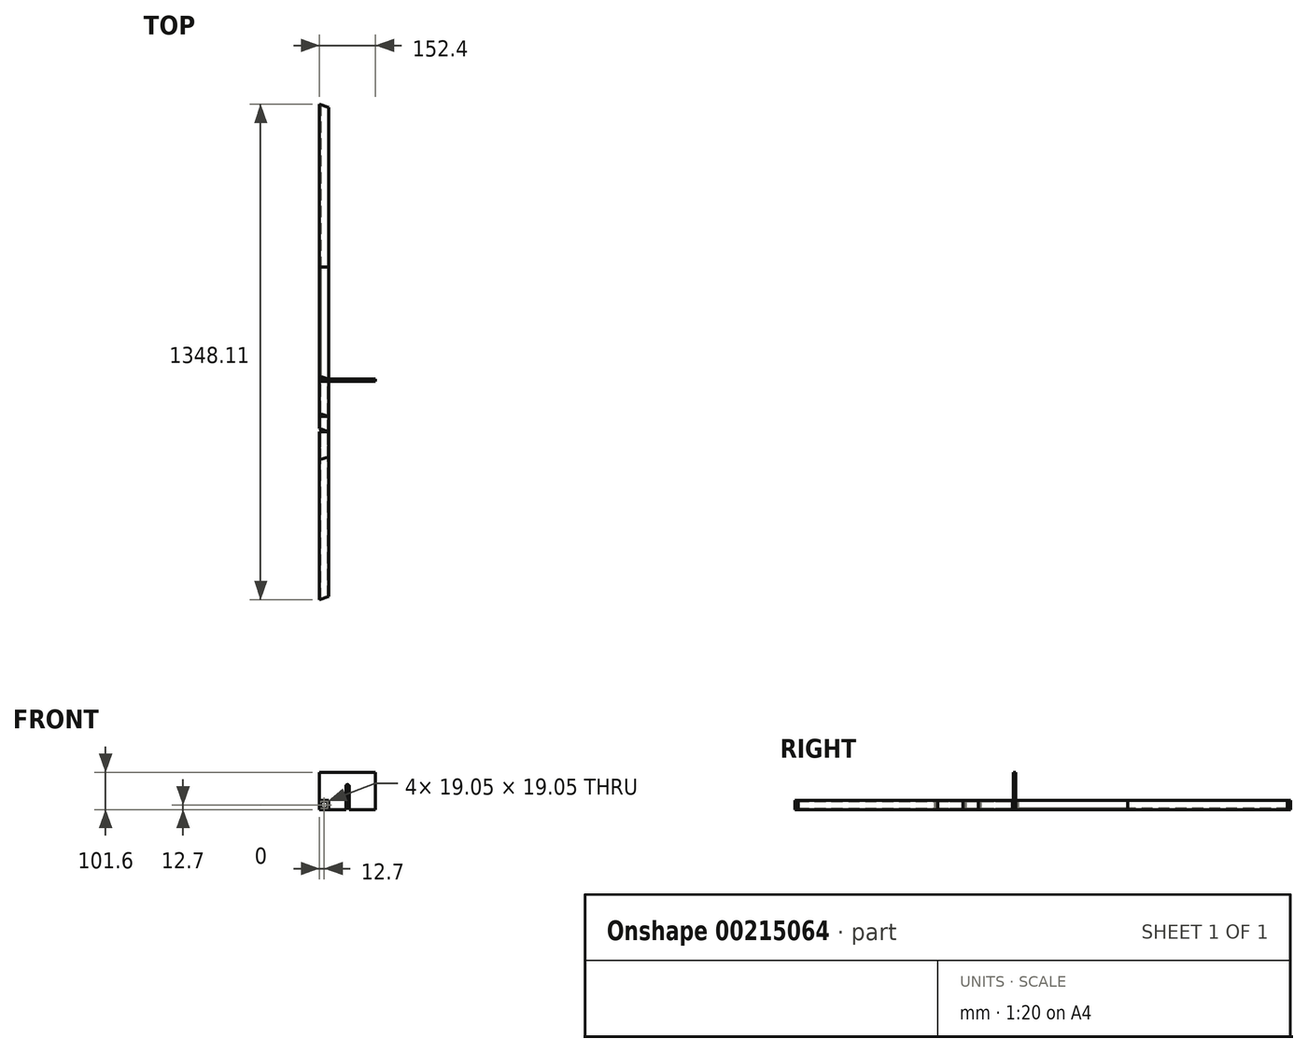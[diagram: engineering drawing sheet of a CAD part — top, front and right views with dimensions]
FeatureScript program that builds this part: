
annotation { "Feature Type Name" : "Feature", "Feature Type Description" : "" }
export const myFeature = defineFeature(function(context is Context, id is Id, definition is map)
    precondition{}
    {
        {
            var Q0;
            Q0=qCreatedBy(makeId("Front.planeOp"),FACE);
            var sketch = newSketch(context, id + "F0", { "sketchPlane" : qUnion([Q0])});
            skLineSegment(sketch, "E0.bottom", {"start": v(0, 0) * mm, "end": v(25.4, 0) * mm});
            skLineSegment(sketch, "E0.top", {"start": v(0, 25.4) * mm, "end": v(25.4, 25.4) * mm});
            skLineSegment(sketch, "E0.left", {"start": v(0, 0) * mm, "end": v(0, 25.4) * mm});
            skLineSegment(sketch, "E0.right", {"start": v(25.4, 0) * mm, "end": v(25.4, 25.4) * mm});
            skLineSegment(sketch, "E1.bottom", {"start": v(3.18, 3.18) * mm, "end": v(22.23, 3.18) * mm});
            skLineSegment(sketch, "E1.top", {"start": v(3.17, 22.23) * mm, "end": v(22.22, 22.23) * mm});
            skLineSegment(sketch, "E1.left", {"start": v(3.17, 3.18) * mm, "end": v(3.17, 22.23) * mm});
            skLineSegment(sketch, "E1.right", {"start": v(22.23, 3.18) * mm, "end": v(22.22, 22.23) * mm});
            skSolve(sketch);
        }
        {
            var Q0;
            Q0 = qSketchRegion(id + "F0", true);
            extrude(context, id + "F1", {"entities" : qUnion([Q0]), "oppositeDirection" : true, "depth" : 748.03 * mm, "offsetDistance" : 25.4 * mm});
        }
        {
            var Q0;
            Q0=makeQuery(id+"F1.opExtrude","SWEPT_FACE",FACE,{"disambiguationData":[OSD([sQuery(id+"F0.wireOp",EDGE,"E0.top")])]});
            var sketch = newSketch(context, id + "F2", { "sketchPlane" : qUnion([Q0])});
            skLineSegment(sketch, "E2", {"start": v(0, 0) * mm, "end": v(25.4, 0) * mm});
            skLineSegment(sketch, "E3", {"start": v(25.4, 0) * mm, "end": v(0, 8.25) * mm});
            skLineSegment(sketch, "E4", {"start": v(0, 8.25) * mm, "end": v(0, 0) * mm});
            skLineSegment(sketch, "E5", {"start": v(25.4, 748.03) * mm, "end": v(0, 748.03) * mm});
            skLineSegment(sketch, "E6", {"start": v(0, 748.03) * mm, "end": v(25.4, 739.78) * mm});
            skLineSegment(sketch, "E7", {"start": v(25.4, 739.78) * mm, "end": v(25.4, 748.03) * mm});
            skSolve(sketch);
        }
        {
            var Q0;
            Q0 = qSketchRegion(id + "F2", true);
            var Q1;
            Q1=makeQuery(id+"F1.opExtrude","SWEPT_FACE",FACE,{"disambiguationData":[OSD([sQuery(id+"F0.wireOp",EDGE,"E0.bottom")])]});
            extrude(context, id + "F3", {"entities" : qUnion([Q0]), "operationType" : NewBodyOperationType.REMOVE, "endBound" : BoundingType.UP_TO_SURFACE, "oppositeDirection" : true, "depth" : 25.4 * mm, "endBoundEntityFace" : qUnion([Q1]), "offsetDistance" : 25.4 * mm});
        }
        {
            var Q0;
            Q0=qCreatedBy(makeId("Front.planeOp"),FACE);
            var sketch = newSketch(context, id + "F4", { "sketchPlane" : qUnion([Q0])});
            skLineSegment(sketch, "E8.bottom", {"start": v(0, 0) * mm, "end": v(25.4, 0) * mm});
            skLineSegment(sketch, "E8.top", {"start": v(0, 25.4) * mm, "end": v(25.4, 25.4) * mm});
            skLineSegment(sketch, "E8.left", {"start": v(0, 0) * mm, "end": v(0, 25.4) * mm});
            skLineSegment(sketch, "E8.right", {"start": v(25.4, 0) * mm, "end": v(25.4, 25.4) * mm});
            skLineSegment(sketch, "E9.bottom", {"start": v(3.18, 3.18) * mm, "end": v(22.23, 3.18) * mm});
            skLineSegment(sketch, "E9.top", {"start": v(3.17, 22.22) * mm, "end": v(22.22, 22.22) * mm});
            skLineSegment(sketch, "E9.left", {"start": v(3.17, 3.18) * mm, "end": v(3.17, 22.22) * mm});
            skLineSegment(sketch, "E9.right", {"start": v(22.23, 3.18) * mm, "end": v(22.22, 22.22) * mm});
            skSolve(sketch);
        }
        {
            var Q0;
            Q0 = qSketchRegion(id + "F4", true);
            extrude(context, id + "F5", {"entities" : qUnion([Q0]), "depth" : 219.71 * mm, "offsetDistance" : 25.4 * mm});
        }
        {
            var Q0;
            Q0=makeQuery(id+"F5.opExtrude","SWEPT_FACE",FACE,{"disambiguationData":[OSD([sQuery(id+"F4.wireOp",EDGE,"E8.top")])]});
            var sketch = newSketch(context, id + "F6", { "sketchPlane" : qUnion([Q0])});
            skLineSegment(sketch, "E10", {"start": v(0, -219.71) * mm, "end": v(25.4, -219.71) * mm});
            skLineSegment(sketch, "E11", {"start": v(25.4, -219.71) * mm, "end": v(25.4, -211.46) * mm});
            skLineSegment(sketch, "E12", {"start": v(25.4, -211.46) * mm, "end": v(0, -219.71) * mm});
            skLineSegment(sketch, "E13", {"start": v(25.4, 0) * mm, "end": v(25.4, -8.25) * mm});
            skLineSegment(sketch, "E14", {"start": v(25.4, -8.25) * mm, "end": v(0, 0) * mm});
            skLineSegment(sketch, "E15", {"start": v(0, 0) * mm, "end": v(25.4, 0) * mm});
            skSolve(sketch);
        }
        {
            var Q0;
            Q0 = qSketchRegion(id + "F6", true);
            var Q1;
            Q1=makeQuery(id+"F5.opExtrude","SWEPT_FACE",FACE,{"disambiguationData":[OSD([sQuery(id+"F4.wireOp",EDGE,"E8.bottom")])]});
            extrude(context, id + "F7", {"entities" : qUnion([Q0]), "operationType" : NewBodyOperationType.REMOVE, "endBound" : BoundingType.UP_TO_SURFACE, "oppositeDirection" : true, "depth" : 25.4 * mm, "endBoundEntityFace" : qUnion([Q1]), "offsetDistance" : 25.4 * mm});
        }
        {
            var Q0;
            Q0=qCreatedBy(makeId("Front.planeOp"),FACE);
            var sketch = newSketch(context, id + "F8", { "sketchPlane" : qUnion([Q0])});
            skLineSegment(sketch, "E16.bottom", {"start": v(0, 0) * mm, "end": v(25.4, 0) * mm});
            skLineSegment(sketch, "E16.top", {"start": v(0, 25.4) * mm, "end": v(25.4, 25.4) * mm});
            skLineSegment(sketch, "E16.left", {"start": v(0, 0) * mm, "end": v(0, 25.4) * mm});
            skLineSegment(sketch, "E16.right", {"start": v(25.4, 0) * mm, "end": v(25.4, 25.4) * mm});
            skLineSegment(sketch, "E17.bottom", {"start": v(3.17, 3.18) * mm, "end": v(22.22, 3.18) * mm});
            skLineSegment(sketch, "E17.top", {"start": v(3.17, 22.22) * mm, "end": v(22.22, 22.22) * mm});
            skLineSegment(sketch, "E17.left", {"start": v(3.17, 3.18) * mm, "end": v(3.17, 22.22) * mm});
            skLineSegment(sketch, "E17.right", {"start": v(22.22, 3.18) * mm, "end": v(22.22, 22.22) * mm});
            skSolve(sketch);
        }
        {
            var Q0;
            Q0 = qSketchRegion(id + "F8", true);
            extrude(context, id + "F9", {"entities" : qUnion([Q0]), "oppositeDirection" : true, "depth" : 304.8 * mm, "offsetDistance" : 25.4 * mm});
        }
        {
            var Q0;
            Q0=qCreatedBy(makeId("Front.planeOp"),FACE);
            var sketch = newSketch(context, id + "F10", { "sketchPlane" : qUnion([Q0])});
            skLineSegment(sketch, "E18.bottom", {"start": v(0, 0) * mm, "end": v(25.4, 0) * mm});
            skLineSegment(sketch, "E18.top", {"start": v(0, 25.4) * mm, "end": v(25.4, 25.4) * mm});
            skLineSegment(sketch, "E18.left", {"start": v(0, 0) * mm, "end": v(0, 25.4) * mm});
            skLineSegment(sketch, "E18.right", {"start": v(25.4, 0) * mm, "end": v(25.4, 25.4) * mm});
            skLineSegment(sketch, "E19.bottom", {"start": v(3.17, 22.22) * mm, "end": v(22.22, 22.22) * mm});
            skLineSegment(sketch, "E19.top", {"start": v(3.17, 3.18) * mm, "end": v(22.22, 3.18) * mm});
            skLineSegment(sketch, "E19.left", {"start": v(3.17, 22.22) * mm, "end": v(3.17, 3.18) * mm});
            skLineSegment(sketch, "E19.right", {"start": v(22.22, 22.22) * mm, "end": v(22.23, 3.18) * mm});
            skSolve(sketch);
        }
        {
            var Q0;
            Q0 = qSketchRegion(id + "F10", true);
            extrude(context, id + "F11", {"entities" : qUnion([Q0]), "depth" : 600.07 * mm, "offsetDistance" : 25.4 * mm});
        }
        {
            var Q0;
            Q0=makeQuery(id+"F11.opExtrude","SWEPT_FACE",FACE,{"disambiguationData":[OSD([sQuery(id+"F10.wireOp",EDGE,"E18.top")])]});
            var sketch = newSketch(context, id + "F12", { "sketchPlane" : qUnion([Q0])});
            skLineSegment(sketch, "E20", {"start": v(0, 0) * mm, "end": v(25.4, -8.25) * mm});
            skLineSegment(sketch, "E21", {"start": v(25.4, -8.25) * mm, "end": v(25.4, 0) * mm});
            skLineSegment(sketch, "E22", {"start": v(25.4, 0) * mm, "end": v(0, 0) * mm});
            skLineSegment(sketch, "E23", {"start": v(0, -600.08) * mm, "end": v(25.4, -591.82) * mm});
            skLineSegment(sketch, "E24", {"start": v(25.4, -591.82) * mm, "end": v(25.4, -600.08) * mm});
            skLineSegment(sketch, "E25", {"start": v(25.4, -600.08) * mm, "end": v(0, -600.08) * mm});
            skSolve(sketch);
        }
        {
            var Q0;
            Q0 = qSketchRegion(id + "F12", true);
            var Q1;
            Q1=makeQuery(id+"F11.opExtrude","SWEPT_FACE",FACE,{"disambiguationData":[OSD([sQuery(id+"F10.wireOp",EDGE,"E18.bottom")])]});
            extrude(context, id + "F13", {"entities" : qUnion([Q0]), "operationType" : NewBodyOperationType.REMOVE, "endBound" : BoundingType.UP_TO_SURFACE, "oppositeDirection" : true, "depth" : 25.4 * mm, "endBoundEntityFace" : qUnion([Q1]), "offsetDistance" : 25.4 * mm});
        }
        {
            var Q0;
            Q0=qCreatedBy(makeId("Front.planeOp"),FACE);
            var sketch = newSketch(context, id + "F14", { "sketchPlane" : qUnion([Q0])});
            skLineSegment(sketch, "E26.bottom", {"start": v(0, 0) * mm, "end": v(25.4, 0) * mm});
            skLineSegment(sketch, "E26.top", {"start": v(0, 25.4) * mm, "end": v(25.4, 25.4) * mm});
            skLineSegment(sketch, "E26.left", {"start": v(0, 0) * mm, "end": v(0, 25.4) * mm});
            skLineSegment(sketch, "E26.right", {"start": v(25.4, 0) * mm, "end": v(25.4, 25.4) * mm});
            skLineSegment(sketch, "E27.bottom", {"start": v(3.18, 3.17) * mm, "end": v(22.22, 3.17) * mm});
            skLineSegment(sketch, "E27.top", {"start": v(3.17, 22.22) * mm, "end": v(22.22, 22.22) * mm});
            skLineSegment(sketch, "E27.left", {"start": v(3.18, 3.18) * mm, "end": v(3.17, 22.22) * mm});
            skLineSegment(sketch, "E27.right", {"start": v(22.22, 3.18) * mm, "end": v(22.22, 22.22) * mm});
            skSolve(sketch);
        }
        {
            var Q0;
            Q0 = qSketchRegion(id + "F14", true);
            extrude(context, id + "F15", {"entities" : qUnion([Q0]), "depth" : 101.58 * mm, "offsetDistance" : 25.4 * mm});
        }
        {
            var Q0;
            Q0=makeQuery(id+"F15.opExtrude","SWEPT_FACE",FACE,{"disambiguationData":[OSD([sQuery(id+"F14.wireOp",EDGE,"E26.top")])]});
            var sketch = newSketch(context, id + "F16", { "sketchPlane" : qUnion([Q0])});
            skLineSegment(sketch, "E28", {"start": v(25.4, -101.58) * mm, "end": v(0, -101.58) * mm});
            skLineSegment(sketch, "E29", {"start": v(0, -101.58) * mm, "end": v(0, -93.33) * mm});
            skLineSegment(sketch, "E30", {"start": v(0, -93.33) * mm, "end": v(25.4, -101.58) * mm});
            skSolve(sketch);
        }
        {
            var Q0;
            Q0 = qSketchRegion(id + "F16", true);
            extrude(context, id + "F17", {"entities" : qUnion([Q0]), "operationType" : NewBodyOperationType.REMOVE, "endBound" : BoundingType.THROUGH_ALL, "oppositeDirection" : true, "depth" : 25.4 * mm, "offsetDistance" : 25.4 * mm});
        }
        {
            var Q0;
            Q0=qCreatedBy(makeId("Front.planeOp"),FACE);
            var sketch = newSketch(context, id + "F18", { "sketchPlane" : qUnion([Q0])});
            skLineSegment(sketch, "E31.bottom", {"start": v(0, 0) * mm, "end": v(25.4, 0) * mm});
            skLineSegment(sketch, "E31.top", {"start": v(0, 25.4) * mm, "end": v(25.4, 25.4) * mm});
            skLineSegment(sketch, "E31.left", {"start": v(0, 0) * mm, "end": v(0, 25.4) * mm});
            skLineSegment(sketch, "E31.right", {"start": v(25.4, 0) * mm, "end": v(25.4, 25.4) * mm});
            skLineSegment(sketch, "E32.bottom", {"start": v(22.22, 22.22) * mm, "end": v(3.17, 22.22) * mm});
            skLineSegment(sketch, "E32.top", {"start": v(22.22, 3.18) * mm, "end": v(3.18, 3.17) * mm});
            skLineSegment(sketch, "E32.left", {"start": v(22.22, 22.22) * mm, "end": v(22.23, 3.18) * mm});
            skLineSegment(sketch, "E32.right", {"start": v(3.17, 22.22) * mm, "end": v(3.17, 3.17) * mm});
            skSolve(sketch);
        }
        {
            var Q0;
            Q0 = qSketchRegion(id + "F18", true);
            extrude(context, id + "F19", {"entities" : qUnion([Q0]), "depth" : 142.84 * mm, "offsetDistance" : 25.4 * mm});
        }
        {
            var Q0;
            Q0=makeQuery(id+"F19.opExtrude","SWEPT_FACE",FACE,{"disambiguationData":[OSD([sQuery(id+"F18.wireOp",EDGE,"E31.top")])]});
            var sketch = newSketch(context, id + "F20", { "sketchPlane" : qUnion([Q0])});
            skLineSegment(sketch, "E33", {"start": v(25.4, -142.84) * mm, "end": v(0, -134.6) * mm});
            skLineSegment(sketch, "E34", {"start": v(0, -134.6) * mm, "end": v(0, -142.84) * mm});
            skLineSegment(sketch, "E35", {"start": v(0, -142.84) * mm, "end": v(25.4, -142.84) * mm});
            skSolve(sketch);
        }
        {
            var Q0;
            Q0 = qSketchRegion(id + "F20", true);
            extrude(context, id + "F21", {"entities" : qUnion([Q0]), "operationType" : NewBodyOperationType.REMOVE, "endBound" : BoundingType.THROUGH_ALL, "oppositeDirection" : true, "depth" : 25.4 * mm, "offsetDistance" : 25.4 * mm});
        }
        {
            var Q0;
            Q0=qCreatedBy(makeId("Front.planeOp"),FACE);
            var sketch = newSketch(context, id + "F22", { "sketchPlane" : qUnion([Q0])});
            skLineSegment(sketch, "E36.bottom", {"start": v(0, 0) * mm, "end": v(71.44, 0) * mm});
            skLineSegment(sketch, "E36.top", {"start": v(0, 101.6) * mm, "end": v(152.4, 101.6) * mm});
            skLineSegment(sketch, "E36.left", {"start": v(0, 0) * mm, "end": v(0, 101.6) * mm});
            skLineSegment(sketch, "E36.right", {"start": v(152.4, 0) * mm, "end": v(152.4, 101.6) * mm});
            skLineSegment(sketch, "E37", {"start": v(71.44, 0) * mm, "end": v(71.44, 63.5) * mm});
            skLineSegment(sketch, "E38", {"start": v(80.96, 63.5) * mm, "end": v(80.96, 0) * mm});
            skArc(sketch, "E39", {"start": v(80.96, 63.5) * mm, "mid": v(76.2, 68.26) * mm, "end": v(71.44, 63.5) * mm});
            skLineSegment(sketch, "E40.trimOffspring", {"start": v(80.96, 0) * mm, "end": v(152.4, 0) * mm});
            skSolve(sketch);
        }
        {
            var Q0;
            Q0 = qSketchRegion(id + "F22", true);
            extrude(context, id + "F23", {"entities" : qUnion([Q0]), "depth" : 6.35 * mm, "offsetDistance" : 25.4 * mm});
        }
    });
